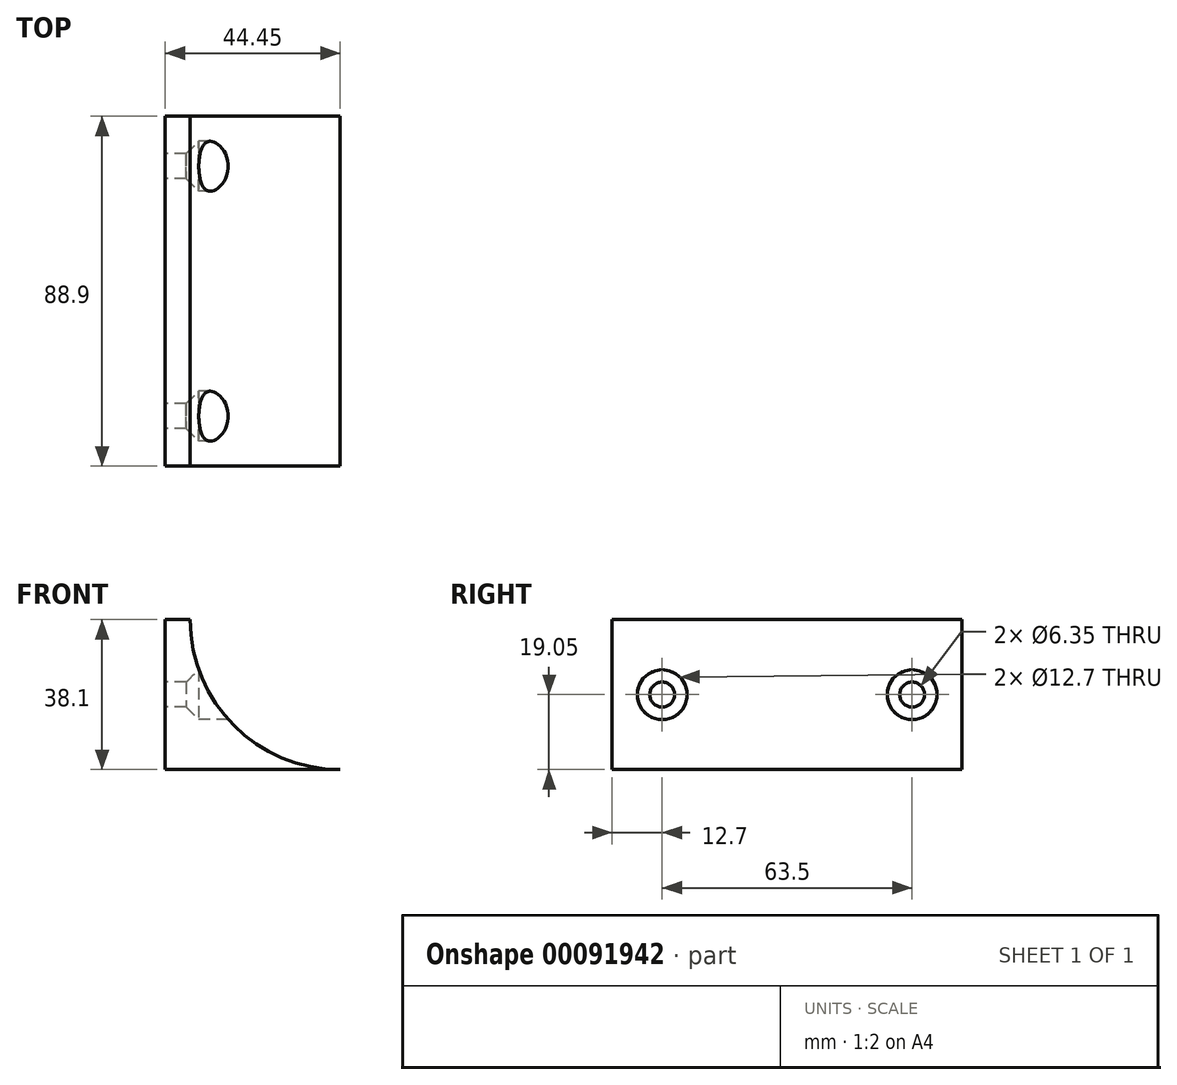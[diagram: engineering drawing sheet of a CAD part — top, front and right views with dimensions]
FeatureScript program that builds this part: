
annotation { "Feature Type Name" : "Feature", "Feature Type Description" : "" }
export const myFeature = defineFeature(function(context is Context, id is Id, definition is map)
    precondition{}
    {
        {
            var Q0;
            Q0=qCreatedBy(makeId("Front.planeOp"),FACE);
            var sketch = newSketch(context, id + "F0", { "sketchPlane" : qUnion([Q0])});
            skArc(sketch, "E0", {"start": v(-38.1, 0) * mm, "mid": v(-26.94, -26.94) * mm, "end": v(0, -38.1) * mm});
            skLineSegment(sketch, "E1", {"start": v(-38.1, 0) * mm, "end": v(-44.45, 0) * mm});
            skLineSegment(sketch, "E2", {"start": v(-44.45, 0) * mm, "end": v(-44.45, -38.1) * mm});
            skLineSegment(sketch, "E3", {"start": v(-44.45, -38.1) * mm, "end": v(0, -38.1) * mm});
            skSolve(sketch);
        }
        {
            var Q0;
            Q0=makeQuery(id+"F0.imprint","IMPRINT",FACE,{"disambiguationData":[TD([[makeQuery(id+"F0.imprint","IMPRINT",EDGE,{"derivedFrom":sQuery(id+"F0.wireOp",EDGE,"E0")}),-1.0]])]});
            extrude(context, id + "F1", {"entities" : qUnion([Q0]), "depth" : 88.9 * mm, "symmetric" : true});
        }
        {
            var Q0;
            Q0=qCreatedBy(makeId("Right.planeOp"),FACE);
            var sketch = newSketch(context, id + "F2", { "sketchPlane" : qUnion([Q0])});
            skCircle(sketch, "E4", {"center": v(-31.75, -19.05) * mm, "radius": 3.5 * mm});
            skCircle(sketch, "E5", {"center": v(31.75, -19.05) * mm, "radius": 3.5 * mm});
            skSolve(sketch);
        }
        {
            var Q0;
            Q0=sQuery(id+"F2.wireOp",VERTEX,"E4.center");
            var Q1;
            Q1=sQuery(id+"F2.wireOp",VERTEX,"E5.center");
            var Q2;
            Q2=makeQuery(id+"F1.opExtrude","SWEPT_BODY",BODY,{"disambiguationData":[OSD([sQuery(id+"F0.wireOp",EDGE,"E0"),sQuery(id+"F0.wireOp",EDGE,"E1"),sQuery(id+"F0.wireOp",EDGE,"E2"),sQuery(id+"F0.wireOp",EDGE,"E3")])]});
            hole(context, id + "F3", {"style" : HoleStyle.C_SINK, "endStyle" : HoleEndStyle.THROUGH, "holeDiameter" : 6.35 * mm, "cSinkDiameter" : 12.7 * mm, "cSinkAngle" : 90 * degree, "locations" : qUnion([Q0, Q1]), "scope" : qUnion([Q2]), "isTappedThrough" : true});
        }
    });
